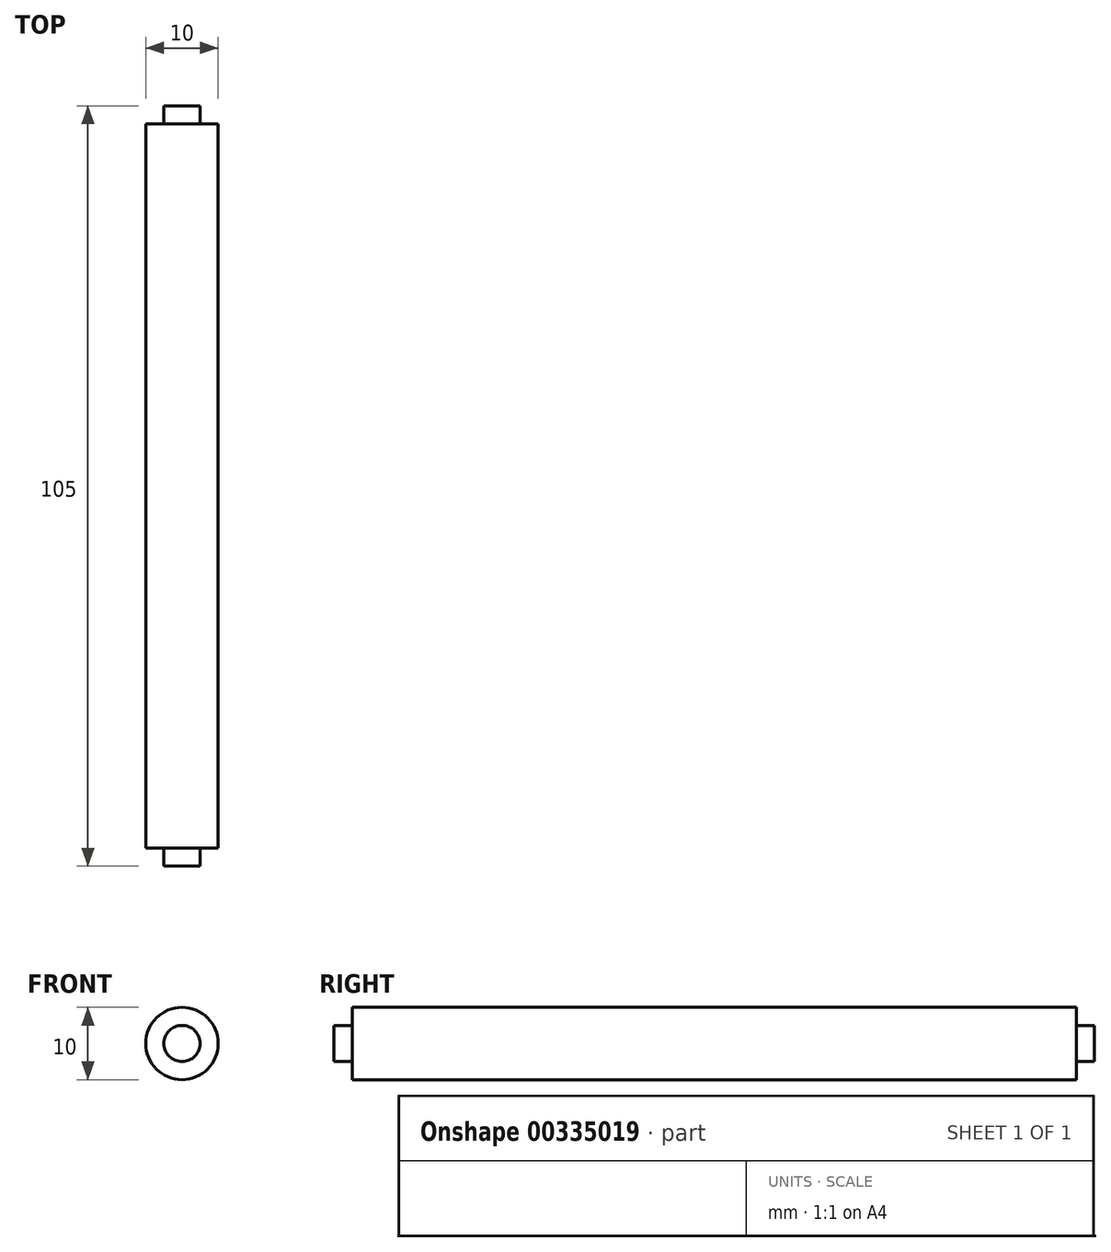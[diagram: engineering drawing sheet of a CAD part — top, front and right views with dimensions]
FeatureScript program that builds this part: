
annotation { "Feature Type Name" : "Feature", "Feature Type Description" : "" }
export const myFeature = defineFeature(function(context is Context, id is Id, definition is map)
    precondition{}
    {
        {
            var Q0;
            Q0=qCreatedBy(makeId("Front.planeOp"),FACE);
            var sketch = newSketch(context, id + "F0", { "sketchPlane" : qUnion([Q0])});
            skCircle(sketch, "E0", {"center": v(0, 0) * mm, "radius": 5 * mm});
            skSolve(sketch);
        }
        {
            var Q0;
            Q0 = qSketchRegion(id + "F0", true);
            extrude(context, id + "F1", {"entities" : qUnion([Q0]), "depth" : 100 * mm});
        }
        {
            var Q0;
            Q0=makeQuery(id+"F1.opExtrude","CAP_FACE",FACE,{"disambiguationData":[OSD([sQuery(id+"F0.wireOp",EDGE,"E0")])],"isStart":false});
            var sketch = newSketch(context, id + "F2", { "sketchPlane" : qUnion([Q0])});
            skCircle(sketch, "E1", {"center": v(0, 0) * mm, "radius": 2.5 * mm});
            skSolve(sketch);
        }
        {
            var Q0;
            Q0=makeQuery(id+"F2.imprint","IMPRINT",FACE,{"disambiguationData":[TD([[makeQuery(id+"F2.imprint","IMPRINT",EDGE,{"derivedFrom":sQuery(id+"F2.wireOp",EDGE,"E1")}),1.0]])]});
            extrude(context, id + "F3", {"entities" : qUnion([Q0]), "operationType" : NewBodyOperationType.ADD, "depth" : 2.5 * mm, "hasSecondDirection" : true, "secondDirectionOppositeDirection" : true, "secondDirectionDepth" : 102.5 * mm});
        }
    });
